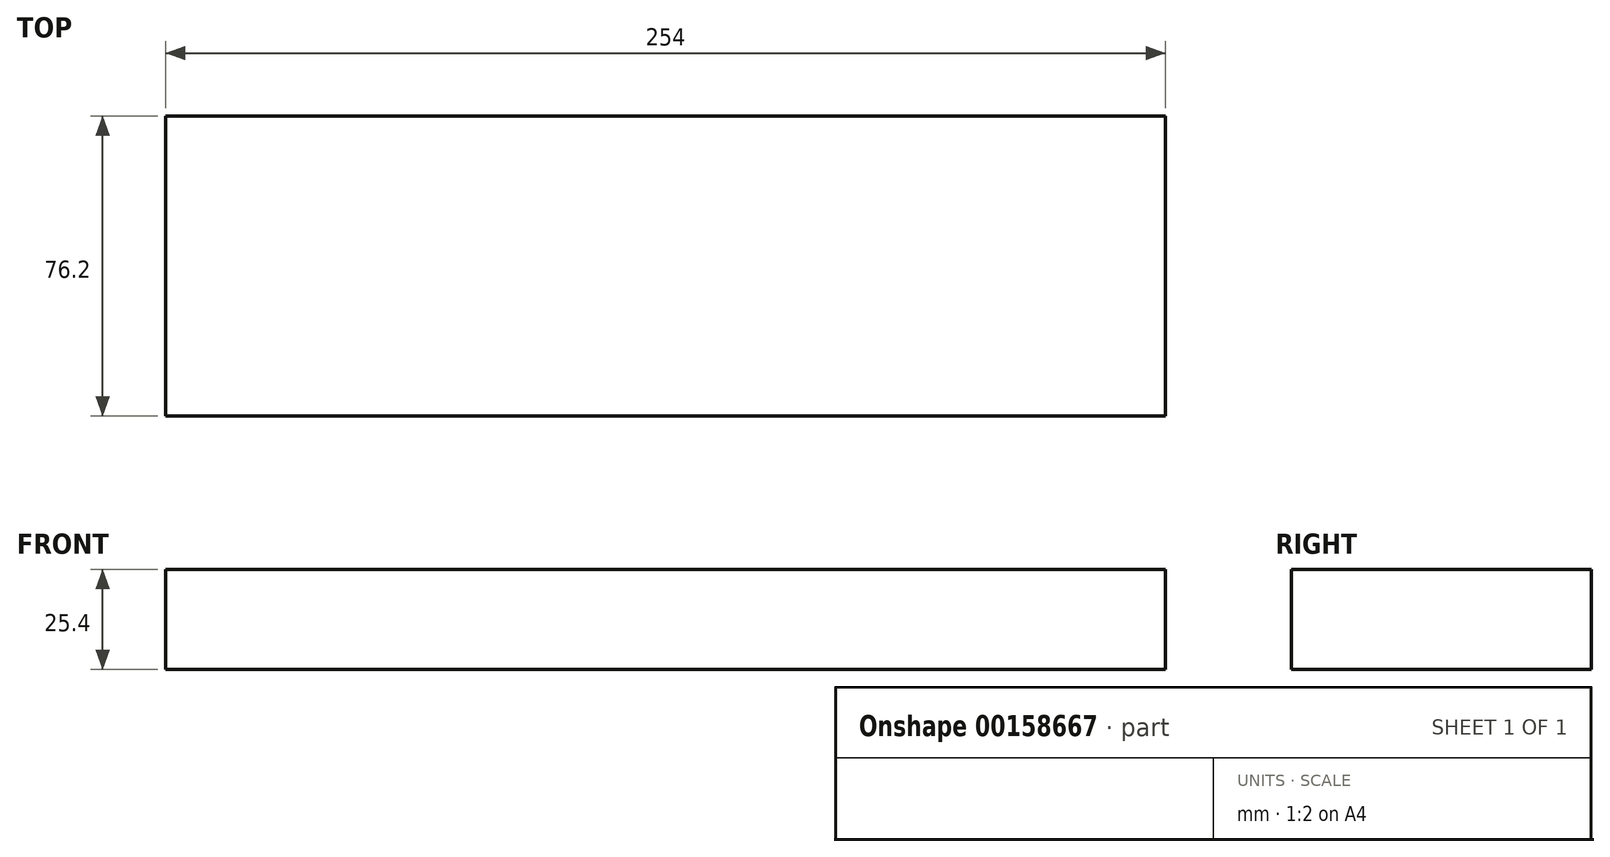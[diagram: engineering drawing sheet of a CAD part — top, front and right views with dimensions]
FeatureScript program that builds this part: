
annotation { "Feature Type Name" : "Feature", "Feature Type Description" : "" }
export const myFeature = defineFeature(function(context is Context, id is Id, definition is map)
    precondition{}
    {
        {
            var Q0;
            Q0=qCreatedBy(makeId("Right.planeOp"),FACE);
            var sketch = newSketch(context, id + "F0", { "sketchPlane" : qUnion([Q0])});
            skLineSegment(sketch, "E0.bottom", {"start": v(-37.06, 16.55) * mm, "end": v(39.14, 16.55) * mm});
            skLineSegment(sketch, "E0.top", {"start": v(-37.06, -8.85) * mm, "end": v(39.14, -8.85) * mm});
            skLineSegment(sketch, "E0.left", {"start": v(-37.06, 16.55) * mm, "end": v(-37.06, -8.85) * mm});
            skLineSegment(sketch, "E0.right", {"start": v(39.14, 16.55) * mm, "end": v(39.14, -8.85) * mm});
            skSolve(sketch);
        }
        {
            var Q0;
            Q0=makeQuery(id+"F0.imprint","IMPRINT",FACE,{"disambiguationData":[TD([[makeQuery(id+"F0.imprint","IMPRINT",EDGE,{"derivedFrom":sQuery(id+"F0.wireOp",EDGE,"E0.bottom")}),-1.0]])]});
            extrude(context, id + "F1", {"entities" : qUnion([Q0]), "depth" : 254 * mm, "hasDraft" : true, "draftAngle" : 0 * degree});
        }
    });
